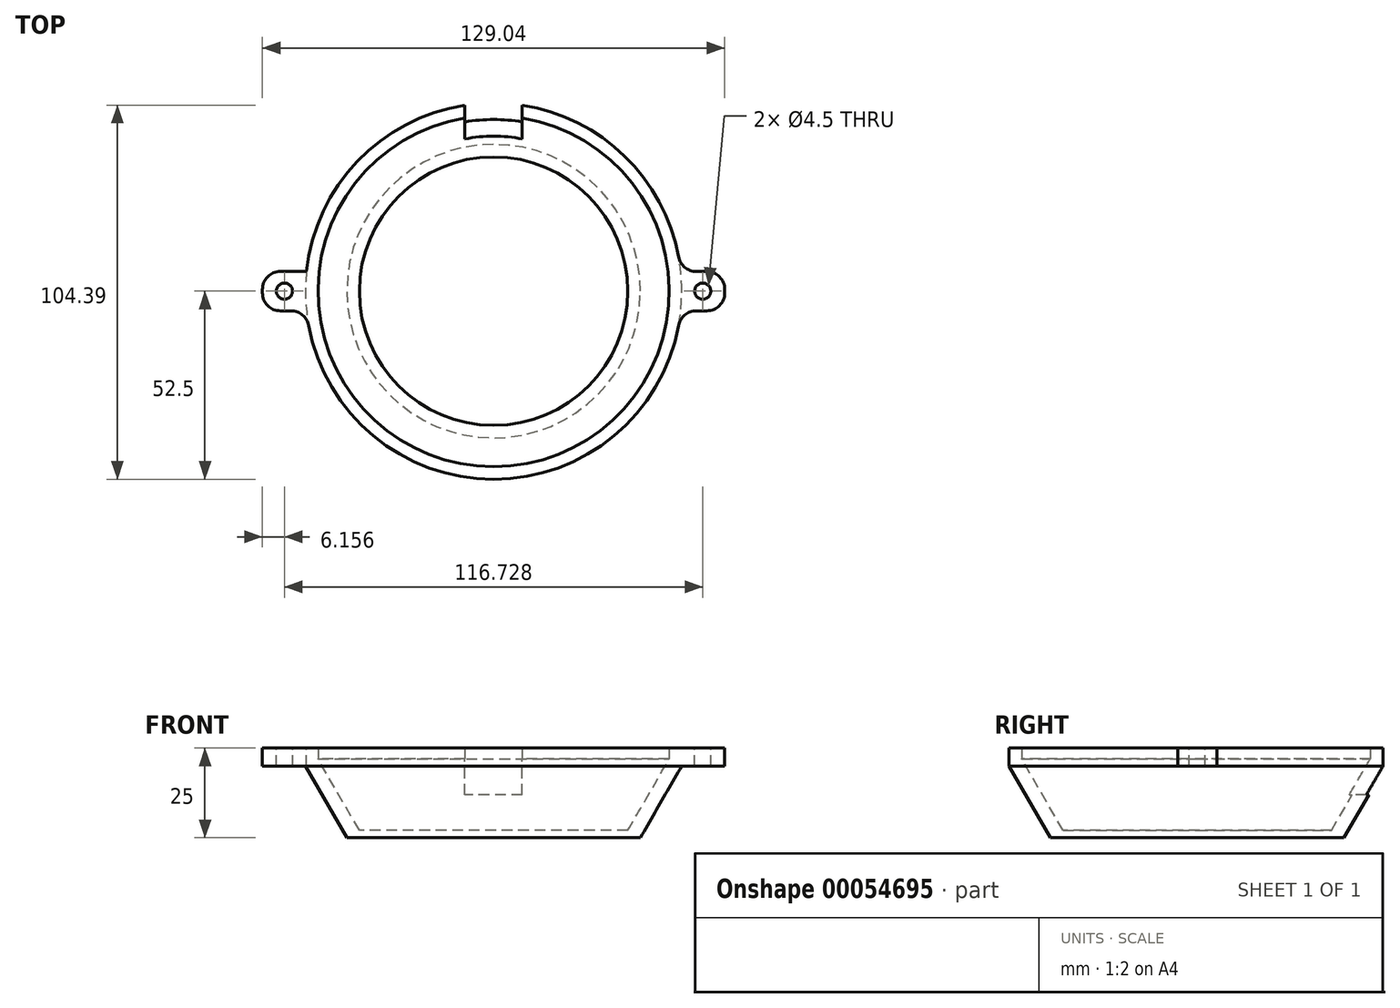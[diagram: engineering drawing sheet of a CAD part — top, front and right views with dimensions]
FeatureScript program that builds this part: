
annotation { "Feature Type Name" : "Feature", "Feature Type Description" : "" }
export const myFeature = defineFeature(function(context is Context, id is Id, definition is map)
    precondition{}
    {
        {
            var Q0;
            Q0=qCreatedBy(makeId("Top.planeOp"),FACE);
            var sketch = newSketch(context, id + "F0", { "sketchPlane" : qUnion([Q0])});
            skCircle(sketch, "E0", {"center": v(0, 0) * mm, "radius": 49 * mm});
            skCircle(sketch, "E1", {"center": v(0, 0) * mm, "radius": 52.5 * mm});
            skSolve(sketch);
        }
        {
            var Q0;
            Q0=makeQuery(id+"F0.imprint","IMPRINT",FACE,{"disambiguationData":[TD([[makeQuery(id+"F0.imprint","IMPRINT",EDGE,{"derivedFrom":sQuery(id+"F0.wireOp",EDGE,"E0")}),-1.0]])]});
            var Q1;
            Q1=makeQuery(id+"F0.imprint","IMPRINT",FACE,{"disambiguationData":[TD([[makeQuery(id+"F0.imprint","IMPRINT",EDGE,{"derivedFrom":sQuery(id+"F0.wireOp",EDGE,"E0")}),1.0]])]});
            extrude(context, id + "F1", {"entities" : qUnion([Q0, Q1]), "depth" : 2 * mm});
        }
        {
            var Q0;
            Q0=makeQuery(id+"F0.imprint","IMPRINT",FACE,{"disambiguationData":[TD([[makeQuery(id+"F0.imprint","IMPRINT",EDGE,{"derivedFrom":sQuery(id+"F0.wireOp",EDGE,"E0")}),-1.0]])]});
            extrude(context, id + "F2", {"entities" : qUnion([Q0]), "operationType" : NewBodyOperationType.ADD, "depth" : 25 * mm});
        }
        {
            var Q0;
            Q0=makeQuery(id+"F2.boolean.opBoolean","INTERSECT",EDGE,{"derivedFrom":[makeQuery(id+"F1.opExtrude","CAP_FACE",FACE,{"disambiguationData":[OSD([sQuery(id+"F0.wireOp",EDGE,"E1")])],"isStart":false}),makeQuery(id+"F2.opExtrude","SWEPT_FACE",FACE,{"disambiguationData":[OSD([sQuery(id+"F0.wireOp",EDGE,"E0")])]})]});
            chamfer(context, id + "F3", {"entities" : qUnion([Q0]), "chamferType" : ChamferType.OFFSET_ANGLE, "width" : 20 * mm, "oppositeDirection" : false, "angle" : 30 * degree, "tangentPropagation" : true});
        }
        {
            var Q0;
            Q0=makeQuery(id+"F1.opExtrude","CAP_EDGE",EDGE,{"disambiguationData":[OSD([sQuery(id+"F0.wireOp",EDGE,"E1")])],"isStart":true});
            chamfer(context, id + "F4", {"entities" : qUnion([Q0]), "chamferType" : ChamferType.OFFSET_ANGLE, "width" : 20 * mm, "oppositeDirection" : false, "angle" : 30 * degree, "tangentPropagation" : true});
        }
        {
            var Q0;
            Q0=makeQuery(id+"F2.opExtrude","CAP_FACE",FACE,{"disambiguationData":[OSD([sQuery(id+"F0.wireOp",EDGE,"E0"),sQuery(id+"F0.wireOp",EDGE,"E1")])],"isStart":false});
            var sketch = newSketch(context, id + "F5", { "sketchPlane" : qUnion([Q0])});
            skLineSegment(sketch, "E2.bottom", {"start": v(8, 67.5) * mm, "end": v(-8, 67.5) * mm});
            skLineSegment(sketch, "E2.top", {"start": v(8, 37.5) * mm, "end": v(-8, 37.5) * mm});
            skLineSegment(sketch, "E2.left", {"start": v(8, 67.5) * mm, "end": v(8, 37.5) * mm});
            skLineSegment(sketch, "E2.right", {"start": v(-8, 67.5) * mm, "end": v(-8, 37.5) * mm});
            skPoint(sketch, "E2.middle", {"position": v(0, 52.5) * mm});
            skSolve(sketch);
        }
        {
            var Q0;
            {var subQ0=sQuery(id+"F5.wireOp",EDGE,"E2.bottom");Q0=makeQuery(id+"F5.imprint","IMPRINT",FACE,{"disambiguationData":[TD([[makeQuery(id+"F5.imprint","IMPRINT",EDGE,{"derivedFrom":subQ0}),1.0]])]});}
            var Q1;
            {var subQ0=sQuery(id+"F5.wireOp",EDGE,"E2.left");var subQ1=sQuery(id+"F0.wireOp",EDGE,"E1");var subQ2=makeQuery(id+"F2.opExtrude","CAP_EDGE",EDGE,{"disambiguationData":[OSD([subQ1])],"isStart":false});var subQ3=makeQuery(id+"F5.imprint","INTERSECT",VERTEX,{"derivedFrom":[subQ2,subQ0]});Q1=makeQuery(id+"F5.imprint","IMPRINT",FACE,{"disambiguationData":[TD([[makeQuery(id+"F5.imprint","IMPRINT",EDGE,{"disambiguationData":[TD([[subQ3,-1.0]])],"derivedFrom":subQ2}),1.0]])]});}
            var Q2;
            {var subQ0=sQuery(id+"F5.wireOp",EDGE,"E2.top");Q2=makeQuery(id+"F5.imprint","IMPRINT",FACE,{"disambiguationData":[TD([[makeQuery(id+"F5.imprint","IMPRINT",EDGE,{"derivedFrom":subQ0}),-1.0]])]});}
            extrude(context, id + "F6", {"entities" : qUnion([Q0, Q1, Q2]), "operationType" : NewBodyOperationType.REMOVE, "oppositeDirection" : true, "depth" : 13 * mm});
        }
        {
            var Q0;
            Q0=makeQuery(id+"F2.opExtrude","CAP_FACE",FACE,{"disambiguationData":[OSD([sQuery(id+"F0.wireOp",EDGE,"E0"),sQuery(id+"F0.wireOp",EDGE,"E1")])],"isStart":false});
            var sketch = newSketch(context, id + "F7", { "sketchPlane" : qUnion([Q0])});
            skLineSegment(sketch, "E3", {"start": v(0, 0) * mm, "end": v(-52.21, -5.49) * mm});
            skLineSegment(sketch, "E4", {"start": v(-52.21, -5.49) * mm, "end": v(-52.21, 5.49) * mm});
            skLineSegment(sketch, "E5", {"start": v(-52.21, 5.49) * mm, "end": v(0, 0) * mm});
            skLineSegment(sketch, "E6", {"start": v(-52.21, -5.49) * mm, "end": v(-64.52, -5.49) * mm});
            skLineSegment(sketch, "E7", {"start": v(-64.52, -5.49) * mm, "end": v(-64.52, 5.49) * mm});
            skLineSegment(sketch, "E8", {"start": v(-64.52, 5.49) * mm, "end": v(-52.21, 5.49) * mm});
            skLineSegment(sketch, "E9", {"start": v(0, -74.25) * mm, "end": v(-74.25, 0) * mm});
            skLineSegment(sketch, "E10", {"start": v(-74.25, 0) * mm, "end": v(0, 74.25) * mm});
            skLineSegment(sketch, "E11", {"start": v(0, -74.25) * mm, "end": v(0, 74.25) * mm});
            skLineSegment(sketch, "E12.MirrorCS", {"start": v(64.52, -5.49) * mm, "end": v(64.52, 5.49) * mm});
            skLineSegment(sketch, "E13.MirrorCS", {"start": v(64.52, 5.49) * mm, "end": v(52.21, 5.49) * mm});
            skCircle(sketch, "E14", {"center": v(-58.36, 0) * mm, "radius": 2.25 * mm});
            skPoint(sketch, "E14.centerSnap0", {"position": v(-64.52, 0) * mm});
            skPoint(sketch, "E14.centerSnap1", {"position": v(-58.36, -5.49) * mm});
            skCircle(sketch, "E15.MirrorC", {"center": v(58.36, 0) * mm, "radius": 2.25 * mm});
            skLineSegment(sketch, "E16.MirrorCS", {"start": v(52.21, -5.49) * mm, "end": v(64.52, -5.49) * mm});
            skSolve(sketch);
        }
        {
            var Q0;
            {var subQ1=sQuery(id+"F7.wireOp",EDGE,"E6");Q0=makeQuery(id+"F7.imprint","IMPRINT",FACE,{"disambiguationData":[TD([[makeQuery(id+"F7.imprint","IMPRINT",EDGE,{"derivedFrom":subQ1}),-1.0]])]});}
            var Q1;
            Q1=makeQuery(id+"F7.imprint","IMPRINT",FACE,{"disambiguationData":[TD([[makeQuery(id+"F7.imprint","IMPRINT",EDGE,{"derivedFrom":sQuery(id+"F7.wireOp",EDGE,"E12.MirrorCS")}),1.0]])]});
            extrude(context, id + "F8", {"entities" : qUnion([Q0, Q1]), "operationType" : NewBodyOperationType.ADD, "oppositeDirection" : true, "depth" : 5 * mm});
        }
        {
            var Q0;
            Q0=makeQuery(id+"F8.opExtrude","SWEPT_EDGE",EDGE,{"disambiguationData":[OSD([sQuery(id+"F7.wireOp",EDGE,"E6"),sQuery(id+"F7.wireOp",EDGE,"E7")])]});
            var Q1;
            Q1=makeQuery(id+"F8.opExtrude","SWEPT_EDGE",EDGE,{"disambiguationData":[OSD([sQuery(id+"F7.wireOp",EDGE,"E7"),sQuery(id+"F7.wireOp",EDGE,"E8")])]});
            var Q2;
            Q2=makeQuery(id+"F8.opExtrude","SWEPT_EDGE",EDGE,{"disambiguationData":[OSD([sQuery(id+"F0.wireOp",EDGE,"E1"),sQuery(id+"F7.wireOp",EDGE,"E3"),sQuery(id+"F7.wireOp",EDGE,"E4"),sQuery(id+"F7.wireOp",EDGE,"E6")])]});
            var Q3;
            Q3=makeQuery(id+"F8.opExtrude","SWEPT_EDGE",EDGE,{"disambiguationData":[OSD([sQuery(id+"F0.wireOp",EDGE,"E1"),sQuery(id+"F7.wireOp",EDGE,"E4"),sQuery(id+"F7.wireOp",EDGE,"E5"),sQuery(id+"F7.wireOp",EDGE,"E8")])]});
            var Q4;
            Q4=makeQuery(id+"F8.opExtrude","SWEPT_EDGE",EDGE,{"disambiguationData":[OSD([sQuery(id+"F0.wireOp",EDGE,"E1"),sQuery(id+"F7.wireOp",EDGE,"E16.MirrorCS")])]});
            var Q5;
            Q5=makeQuery(id+"F8.opExtrude","SWEPT_EDGE",EDGE,{"disambiguationData":[OSD([sQuery(id+"F7.wireOp",EDGE,"E12.MirrorCS"),sQuery(id+"F7.wireOp",EDGE,"E16.MirrorCS")])]});
            var Q6;
            Q6=makeQuery(id+"F8.opExtrude","SWEPT_EDGE",EDGE,{"disambiguationData":[OSD([sQuery(id+"F7.wireOp",EDGE,"E12.MirrorCS"),sQuery(id+"F7.wireOp",EDGE,"E13.MirrorCS")])]});
            var Q7;
            Q7=makeQuery(id+"F8.opExtrude","SWEPT_EDGE",EDGE,{"disambiguationData":[OSD([sQuery(id+"F0.wireOp",EDGE,"E1"),sQuery(id+"F7.wireOp",EDGE,"E13.MirrorCS")])]});
            fillet(context, id + "F9", {"entities" : qUnion([Q0, Q1, Q2, Q3, Q4, Q5, Q6, Q7]), "radius" : 5 * mm, "tangentPropagation" : true, "allowEdgeOverflow" : false});
        }
    });
